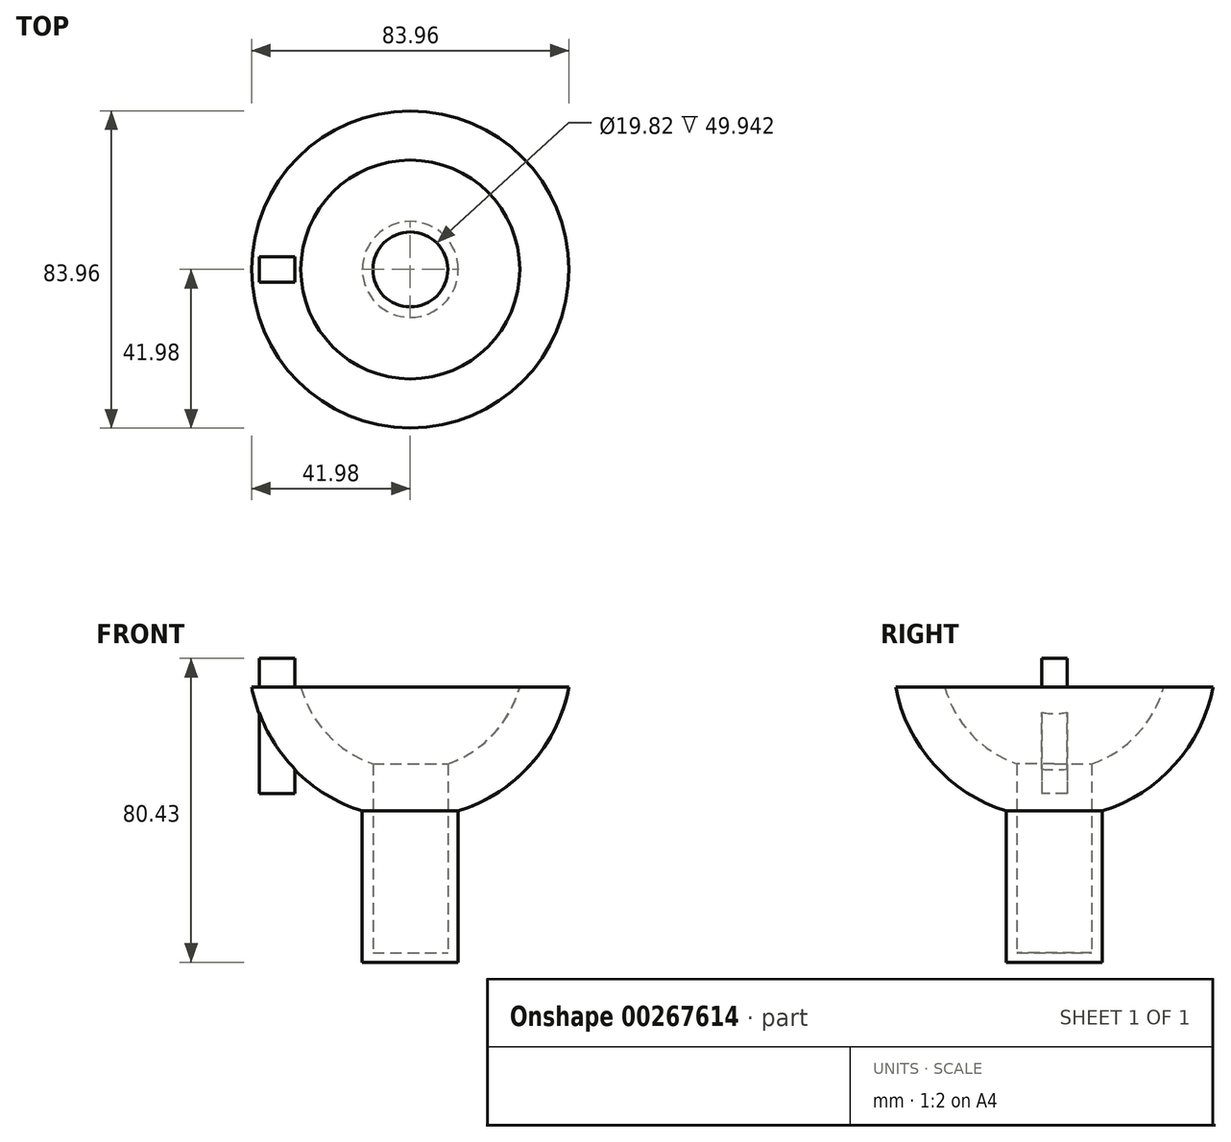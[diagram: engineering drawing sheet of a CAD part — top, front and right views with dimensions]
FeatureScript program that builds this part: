
annotation { "Feature Type Name" : "Feature", "Feature Type Description" : "" }
export const myFeature = defineFeature(function(context is Context, id is Id, definition is map)
    precondition{}
    {
        {
            var Q0;
            Q0=qCreatedBy(makeId("Front.planeOp"),FACE);
            var sketch = newSketch(context, id + "F0", { "sketchPlane" : qUnion([Q0])});
            skLineSegment(sketch, "E0", {"start": v(0, 6.18) * mm, "end": v(0, -44.62) * mm});
            skArc(sketch, "E1", {"start": v(0, 6.18) * mm, "mid": v(18.21, 12.33) * mm, "end": v(28.97, 28.27) * mm});
            skArc(sketch, "E2.0", {"start": v(12.7, -4.59) * mm, "mid": v(31.87, 7.75) * mm, "end": v(41.98, 28.18) * mm});
            skLineSegment(sketch, "E2.1", {"start": v(12.7, -4.59) * mm, "end": v(12.7, -44.62) * mm});
            skLineSegment(sketch, "E3", {"start": v(28.97, 28.27) * mm, "end": v(41.98, 28.18) * mm});
            skLineSegment(sketch, "E4", {"start": v(0, -44.62) * mm, "end": v(12.7, -44.62) * mm});
            skSolve(sketch);
        }
        {
            var Q0;
            Q0 = qSketchRegion(id + "F0", true);
            var Q1;
            Q1=sQuery(id+"F0.wireOp",EDGE,"E0");
            revolve(context, id + "F1", {"entities" : qUnion([Q0]), "axis" : qUnion([Q1]), "revolveType" : RevolveType.FULL});
        }
        {
            var Q0;
            Q0=makeQuery(id+"F1.opRevolve","SWEPT_FACE",FACE,{"disambiguationData":[OSD([sQuery(id+"F0.wireOp",EDGE,"E4")])]});
            var sketch = newSketch(context, id + "F2", { "sketchPlane" : qUnion([Q0])});
            skCircle(sketch, "E5", {"center": v(0, 0) * mm, "radius": 9.91 * mm});
            skSolve(sketch);
        }
        {
            var Q0;
            Q0 = qSketchRegion(id + "F2", true);
            extrude(context, id + "F3", {"entities" : qUnion([Q0]), "operationType" : NewBodyOperationType.REMOVE, "endBound" : BoundingType.THROUGH_ALL, "oppositeDirection" : true, "depth" : 25.4 * mm});
        }
        {
            var Q0;
            Q0 = qSketchRegion(id + "F2", true);
            extrude(context, id + "F4", {"entities" : qUnion([Q0]), "operationType" : NewBodyOperationType.ADD, "oppositeDirection" : true, "depth" : 2.54 * mm});
        }
        {
            var Q0;
            Q0=qCreatedBy(makeId("Top.planeOp"),FACE);
            var sketch = newSketch(context, id + "F5", { "sketchPlane" : qUnion([Q0])});
            skLineSegment(sketch, "E6.bottom", {"start": v(-40, 3.39) * mm, "end": v(-30.55, 3.39) * mm});
            skLineSegment(sketch, "E6.top", {"start": v(-40, -3.39) * mm, "end": v(-30.55, -3.39) * mm});
            skLineSegment(sketch, "E6.left", {"start": v(-40, 3.39) * mm, "end": v(-40, -3.39) * mm});
            skLineSegment(sketch, "E6.right", {"start": v(-30.55, 3.39) * mm, "end": v(-30.55, -3.39) * mm});
            skPoint(sketch, "E6.middle", {"position": v(-35.28, 0) * mm});
            skSolve(sketch);
        }
        {
            var Q0;
            Q0 = qSketchRegion(id + "F5", true);
            extrude(context, id + "F6", {"entities" : qUnion([Q0]), "operationType" : NewBodyOperationType.ADD, "depth" : 35.81 * mm});
        }
    });
